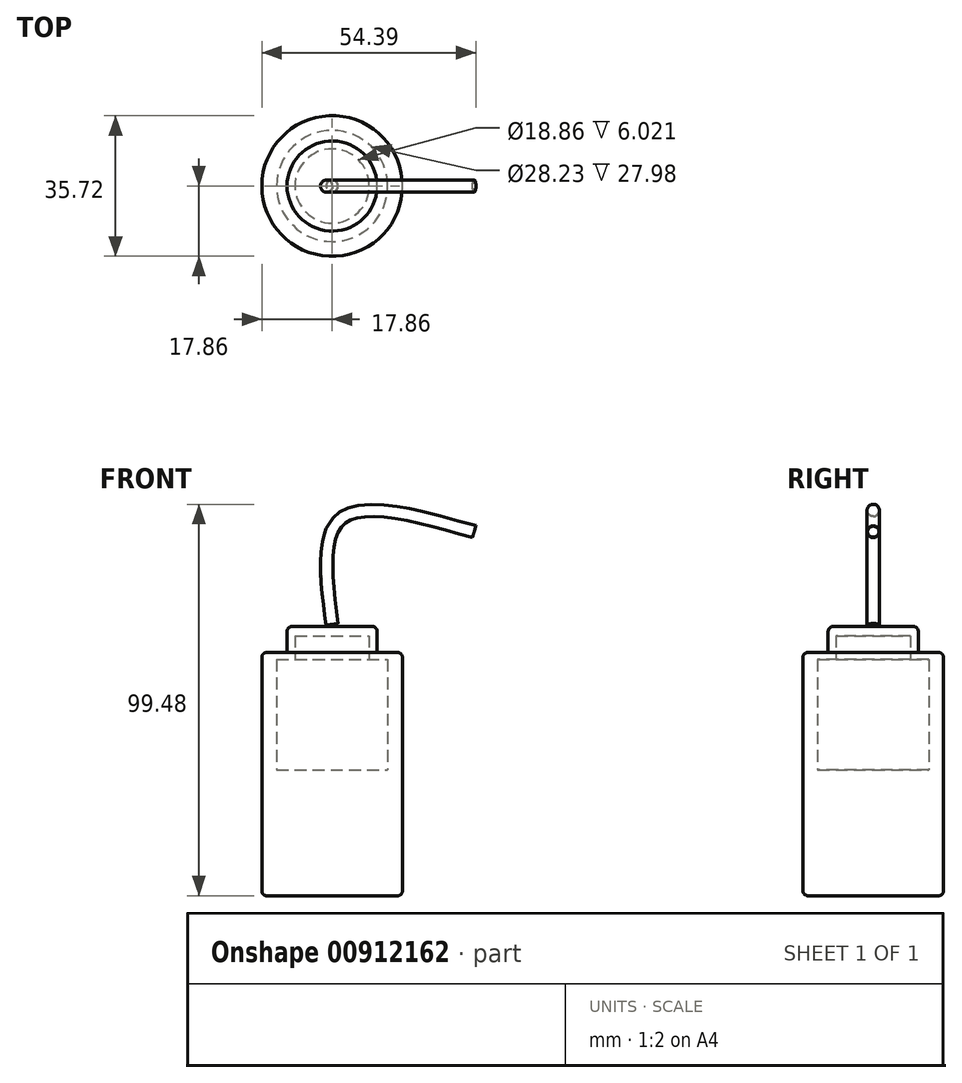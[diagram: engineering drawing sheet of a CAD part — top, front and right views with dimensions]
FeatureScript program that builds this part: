
annotation { "Feature Type Name" : "Feature", "Feature Type Description" : "" }
export const myFeature = defineFeature(function(context is Context, id is Id, definition is map)
    precondition{}
    {
        {
            var Q0;
            Q0=qCreatedBy(makeId("Front.planeOp"),FACE);
            var sketch = newSketch(context, id + "F0", { "sketchPlane" : qUnion([Q0])});
            skLineSegment(sketch, "E0", {"start": v(0, -53.05) * mm, "end": v(16.6, -53.05) * mm});
            skLineSegment(sketch, "E1", {"start": v(17.86, -51.78) * mm, "end": v(17.86, 7.51) * mm});
            skLineSegment(sketch, "E2", {"start": v(16.6, 8.78) * mm, "end": v(11.44, 8.78) * mm});
            skLineSegment(sketch, "E3", {"start": v(11.44, 8.78) * mm, "end": v(11.44, 14.12) * mm});
            skLineSegment(sketch, "E4", {"start": v(10.17, 15.4) * mm, "end": v(0, 15.4) * mm});
            skPoint(sketch, "E5.visualSharp", {"position": v(11.44, 15.4) * mm});
            skArc(sketch, "E5.filletArc", {"start": v(11.44, 14.12) * mm, "mid": v(11.07, 15.02) * mm, "end": v(10.17, 15.4) * mm});
            skPoint(sketch, "E6.visualSharp", {"position": v(17.86, 8.78) * mm});
            skArc(sketch, "E6.filletArc", {"start": v(17.86, 7.51) * mm, "mid": v(17.5, 8.41) * mm, "end": v(16.6, 8.78) * mm});
            skPoint(sketch, "E7.visualSharp", {"position": v(17.86, -53.05) * mm});
            skArc(sketch, "E7.filletArc", {"start": v(16.6, -53.05) * mm, "mid": v(17.5, -52.68) * mm, "end": v(17.86, -51.78) * mm});
            skLineSegment(sketch, "E8", {"start": v(0, -53.05) * mm, "end": v(0, 15.4) * mm, "construction": true});
            skLineSegment(sketch, "E9", {"start": v(0, 15.4) * mm, "end": v(0, 13) * mm});
            skLineSegment(sketch, "E10", {"start": v(0, 13) * mm, "end": v(9.43, 13) * mm});
            skLineSegment(sketch, "E11", {"start": v(9.43, 13) * mm, "end": v(9.43, 6.97) * mm});
            skLineSegment(sketch, "E12", {"start": v(9.43, 6.97) * mm, "end": v(14.11, 6.97) * mm});
            skLineSegment(sketch, "E13", {"start": v(14.11, 6.97) * mm, "end": v(14.11, -21) * mm});
            skLineSegment(sketch, "E14", {"start": v(14.11, -21) * mm, "end": v(0, -21) * mm});
            skLineSegment(sketch, "E15", {"start": v(0, -21) * mm, "end": v(0, -53.05) * mm});
            skSolve(sketch);
        }
        {
            var Q0;
            Q0 = qSketchRegion(id + "F0", true);
            var Q1;
            Q1=sQuery(id+"F0.wireOp",EDGE,"E8");
            revolve(context, id + "F1", {"surfaceOperationType" : NewSurfaceOperationType.NEW, "entities" : qUnion([Q0]), "axis" : qUnion([Q1]), "revolveType" : RevolveType.FULL});
        }
        {
            var Q0;
            Q0=qCreatedBy(makeId("Front.planeOp"),FACE);
            var sketch = newSketch(context, id + "F2", { "sketchPlane" : qUnion([Q0])});
            skFitSpline(sketch, "E16", {"points": [v(0, 15.9) * mm, v(2.15, 42.65) * mm, v(36.1, 39.47) * mm], "startDerivative": vector(-9.4, 71.7) * mm, "endDerivative": vector(79.82, -22.67) * mm});
            skSolve(sketch);
        }
        {
            var Q0;
            Q0=sQuery(id+"F2.wireOp",VERTEX,"E16.start");
            var Q1;
            Q1=sQuery(id+"F2.wireOp",EDGE,"E16");
            cPlane(context, id + "F3", {"entities" : qUnion([Q0, Q1]), "cplaneType" : CPlaneType.CURVE_POINT, "offset" : 25.4 * mm, "width" : 152.4 * mm, "height" : 152.4 * mm});
        }
        {
            var Q0;
            Q0=qCreatedBy(id+"F3.planeOp",FACE);
            var sketch = newSketch(context, id + "F4", { "sketchPlane" : qUnion([Q0])});
            skCircle(sketch, "E17", {"center": v(2.07, 0) * mm, "radius": 1.57 * mm});
            skCircle(sketch, "E18", {"center": v(2.07, 0) * mm, "radius": 1.46 * mm});
            skSolve(sketch);
        }
        {
            var Q0;
            Q0=makeQuery(id+"F4.imprint","IMPRINT",FACE,{"disambiguationData":[TD([[makeQuery(id+"F4.imprint","IMPRINT",EDGE,{"derivedFrom":sQuery(id+"F4.wireOp",EDGE,"E17")}),1.0]])]});
            var Q1;
            Q1=sQuery(id+"F2.wireOp",EDGE,"E16");
            sweep(context, id + "F5", {"profiles" : qUnion([Q0]), "path" : qUnion([Q1])});
        }
    });
